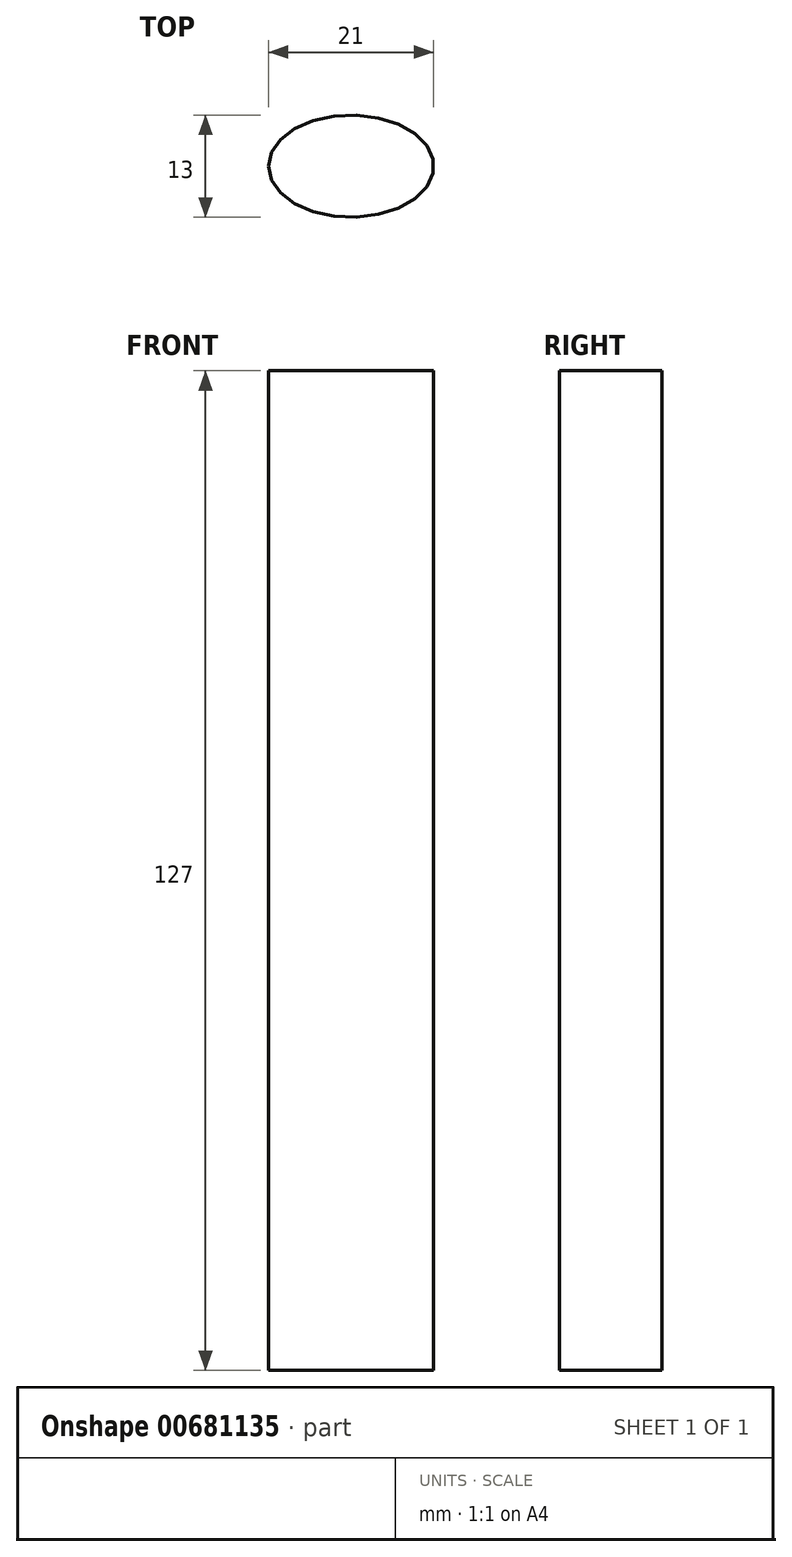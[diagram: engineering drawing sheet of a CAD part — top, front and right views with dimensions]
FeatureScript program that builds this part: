
annotation { "Feature Type Name" : "Feature", "Feature Type Description" : "" }
export const myFeature = defineFeature(function(context is Context, id is Id, definition is map)
    precondition{}
    {
        {
            var Q0;
            Q0=qCreatedBy(makeId("Top.planeOp"),FACE);
            var sketch = newSketch(context, id + "F0", { "sketchPlane" : qUnion([Q0])});
            skEllipse(sketch, "E0", {"center": v(0, 0) * mm, "majorRadius": 10.5 * mm, "minorRadius": 6.5 * mm, "majorAxis": v(-1, 0)});
            skSolve(sketch);
        }
        {
            var Q0;
            Q0=qCreatedBy(makeId("Right.planeOp"),FACE);
            var sketch = newSketch(context, id + "F1", { "sketchPlane" : qUnion([Q0])});
            skLineSegment(sketch, "E1", {"start": v(0, 0) * mm, "end": v(0, -127) * mm});
            skSolve(sketch);
        }
        {
            var Q0;
            Q0=makeQuery(id+"F0.imprint","IMPRINT",FACE,{"disambiguationData":[TD([[makeQuery(id+"F0.imprint","IMPRINT",EDGE,{"derivedFrom":sQuery(id+"F0.wireOp",EDGE,"E0")}),1.0]])]});
            var Q1;
            Q1=sQuery(id+"F1.wireOp",EDGE,"E1");
            sweep(context, id + "F2", {"profiles" : qUnion([Q0]), "path" : qUnion([Q1])});
        }
    });
